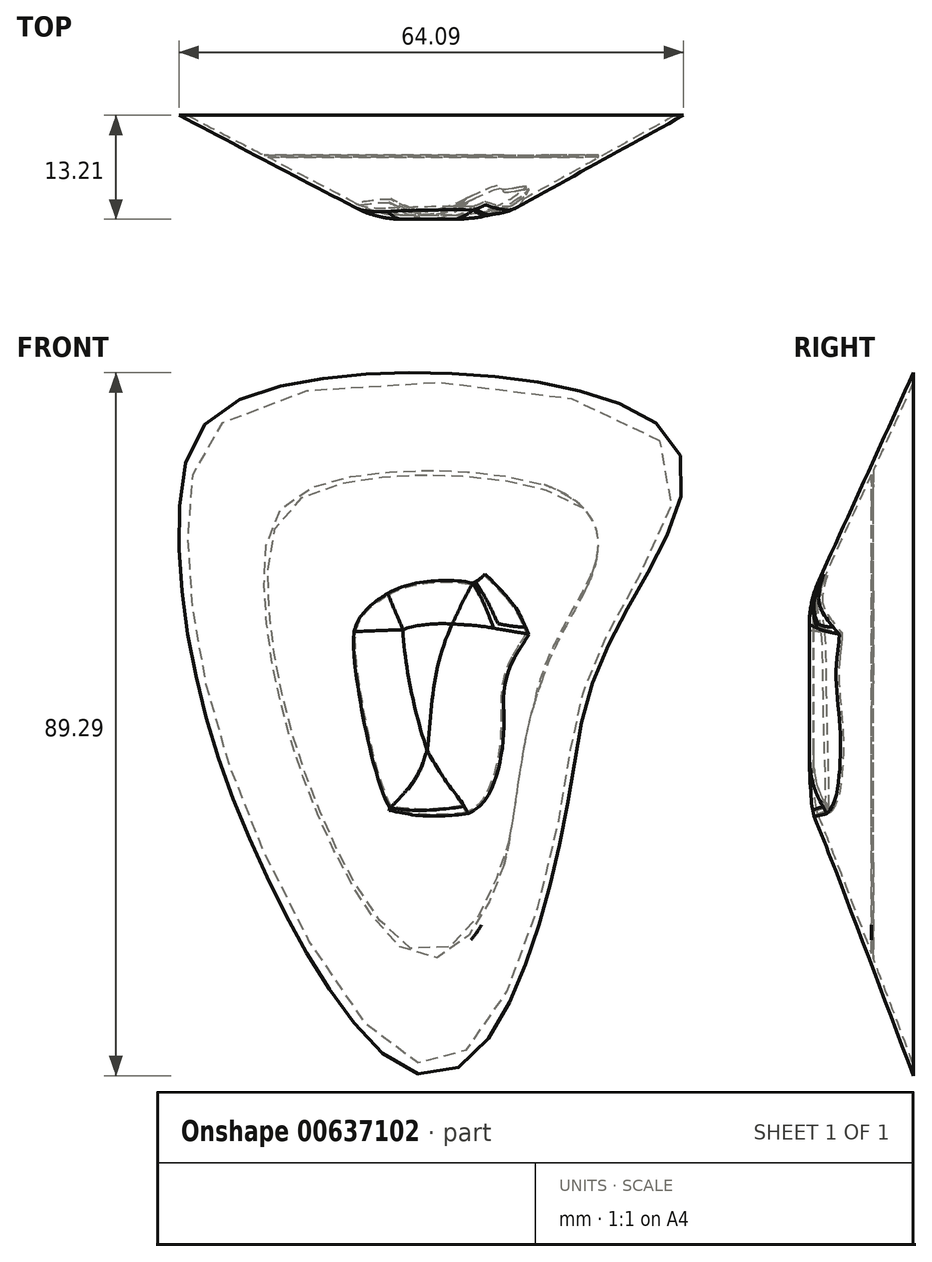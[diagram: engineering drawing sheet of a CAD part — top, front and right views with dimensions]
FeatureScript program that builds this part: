
annotation { "Feature Type Name" : "Feature", "Feature Type Description" : "" }
export const myFeature = defineFeature(function(context is Context, id is Id, definition is map)
    precondition{}
    {
        {
            var Q0;
            Q0=qCreatedBy(makeId("Front.planeOp"),FACE);
            var sketch = newSketch(context, id + "F0", { "sketchPlane" : qUnion([Q0])});
            skFitSpline(sketch, "E0", {"points": [v(18.67, 34.71) * mm, v(-32.85, 39.3) * mm, v(-41.14, 27.5) * mm, v(-40.05, 8.73) * mm, v(-31.32, -18.34) * mm, v(-13.2, -43.88) * mm, v(-3.81, -40.39) * mm, v(5.8, -13.54) * mm, v(8.85, 2.62) * mm, v(15.62, 16.8) * mm, v(18.67, 34.71) * mm]});
            skSolve(sketch);
        }
        {
            var Q0;
            Q0=qCreatedBy(makeId("Front.planeOp"),FACE);
            cPlane(context, id + "F1", {"entities" : qUnion([Q0]), "cplaneType" : CPlaneType.OFFSET, "offset" : 12.7 * mm, "width" : 152.4 * mm, "height" : 152.4 * mm});
        }
        {
            var Q0;
            Q0=qCreatedBy(id+"F1.planeOp",FACE);
            var sketch = newSketch(context, id + "F2", { "sketchPlane" : qUnion([Q0])});
            skFitSpline(sketch, "E1", {"points": [v(-2.73, 12.66) * mm, v(-15.17, 12.88) * mm, v(-16.92, 6.11) * mm, v(-14.74, -4.58) * mm, v(-11.24, -11.35) * mm, v(-6.44, -6.77) * mm, v(-5.13, 0) * mm, v(-4.48, 6.55) * mm, v(-2.73, 12.66) * mm]});
            skSolve(sketch);
        }
        {
            var Q0;
            Q0=makeQuery(id+"F0.imprint","IMPRINT",FACE,{"disambiguationData":[TD([[makeQuery(id+"F0.imprint","IMPRINT",EDGE,{"derivedFrom":sQuery(id+"F0.wireOp",EDGE,"E0")}),1.0]])]});
            var Q1;
            Q1=makeQuery(id+"F2.imprint","IMPRINT",FACE,{"disambiguationData":[TD([[makeQuery(id+"F2.imprint","IMPRINT",EDGE,{"derivedFrom":sQuery(id+"F2.wireOp",EDGE,"E1")}),1.0]])]});
            loft(context, id + "F3", {"sheetProfilesArray" : [{ "sheetProfileEntities" : qUnion([Q0]) }, { "sheetProfileEntities" : qUnion([Q1]) }]});
        }
        {
            var Q0;
            Q0=makeQuery(id+"F3.opLoft","MID_CAP_EDGE",EDGE,{"disambiguationData":[OSD([sQuery(id+"F0.wireOp",EDGE,"E0"),sQuery(id+"F2.wireOp",EDGE,"E1")])],"capPos":1.0});
            fillet(context, id + "F4", {"entities" : qUnion([Q0]), "radius" : 12.7 * mm, "tangentPropagation" : true, "allowEdgeOverflow" : false});
        }
        {
            var Q0;
            Q0=makeQuery(id+"F3.opLoft","CAP_FACE",FACE,{"disambiguationData":[OSD([makeQuery(id+"F0.imprint","IMPRINT",FACE,{"disambiguationData":[TD([[makeQuery(id+"F0.imprint","IMPRINT",EDGE,{"derivedFrom":sQuery(id+"F0.wireOp",EDGE,"E0")}),1.0]])]})])],"isStart":true});
            var Q1;
            Q1=makeQuery(id+"F3.opLoft","SWEPT_BODY",BODY,{"disambiguationData":[OSD([makeQuery(id+"F0.imprint","IMPRINT",FACE,{"disambiguationData":[TD([[makeQuery(id+"F0.imprint","IMPRINT",EDGE,{"derivedFrom":sQuery(id+"F0.wireOp",EDGE,"E0")}),1.0]])]}),makeQuery(id+"F2.imprint","IMPRINT",FACE,{"disambiguationData":[TD([[makeQuery(id+"F2.imprint","IMPRINT",EDGE,{"derivedFrom":sQuery(id+"F2.wireOp",EDGE,"E1")}),1.0]])]})])]});
            shell(context, id + "F5", {"entities" : qUnion([Q0]), "parts" : qUnion([Q1]), "thickness" : 0.5 * mm, "oppositeDirection" : true});
        }
        {
            var Q0;
            Q0=qCreatedBy(id+"F1.planeOp",FACE);
            cPlane(context, id + "F6", {"entities" : qUnion([Q0]), "cplaneType" : CPlaneType.OFFSET, "offset" : 7.62 * mm, "oppositeDirection" : true, "width" : 152.4 * mm, "height" : 152.4 * mm});
        }
        {
            var Q0;
            Q0=qCreatedBy(id+"F6.planeOp",FACE);
            var sketch = newSketch(context, id + "F7", { "sketchPlane" : qUnion([Q0])});
            skFitSpline(sketch, "E2", {"points": [v(3.43, 29.35) * mm, v(-28.56, 27.52) * mm, v(-31.76, 12) * mm, v(-28.49, -3.5) * mm, v(-17.25, -27.36) * mm, v(-10.37, -31.68) * mm, v(-4.48, -27.5) * mm, v(0, -13.32) * mm, v(3.94, 4.98) * mm, v(10.8, 21.34) * mm, v(3.43, 29.35) * mm]});
            skSolve(sketch);
        }
        {
            var Q0;
            Q0 = qSketchRegion(id + "F7", true);
            extrude(context, id + "F8", {"entities" : qUnion([Q0]), "operationType" : NewBodyOperationType.ADD, "depth" : 0.25 * mm, "offsetDistance" : 25.4 * mm});
        }
    });
